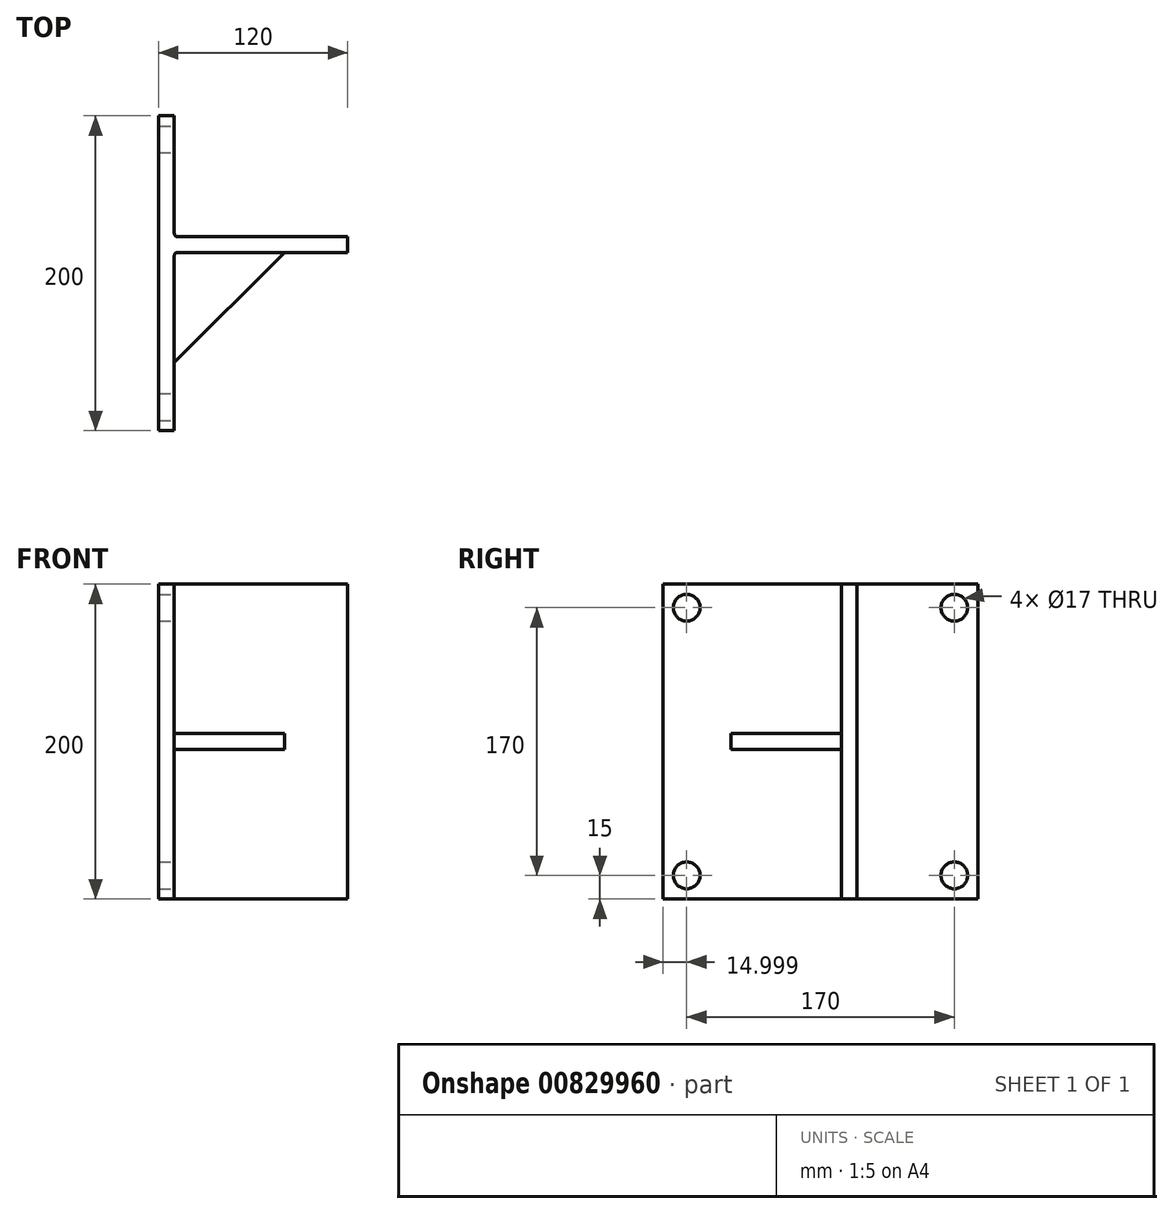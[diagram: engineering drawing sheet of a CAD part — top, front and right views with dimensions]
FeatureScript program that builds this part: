
annotation { "Feature Type Name" : "Feature", "Feature Type Description" : "" }
export const myFeature = defineFeature(function(context is Context, id is Id, definition is map)
    precondition{}
    {
        {
            var Q0;
            Q0=qCreatedBy(makeId("Top.planeOp"),FACE);
            var sketch = newSketch(context, id + "F0", { "sketchPlane" : qUnion([Q0])});
            skLineSegment(sketch, "E0", {"start": v(-22.94, 104.59) * mm, "end": v(-22.94, -95.41) * mm});
            skLineSegment(sketch, "E1", {"start": v(-22.94, -95.41) * mm, "end": v(-12.94, -95.41) * mm});
            skLineSegment(sketch, "E2", {"start": v(-12.94, -95.41) * mm, "end": v(-12.94, 17.79) * mm});
            skLineSegment(sketch, "E3", {"start": v(-12.94, 17.79) * mm, "end": v(97.06, 17.79) * mm});
            skLineSegment(sketch, "E4", {"start": v(-22.94, 104.59) * mm, "end": v(-12.94, 104.59) * mm});
            skLineSegment(sketch, "E5", {"start": v(97.06, 17.79) * mm, "end": v(97.06, 27.79) * mm});
            skLineSegment(sketch, "E6", {"start": v(97.06, 27.79) * mm, "end": v(-12.94, 27.79) * mm});
            skLineSegment(sketch, "E7", {"start": v(-12.94, 104.59) * mm, "end": v(-12.94, 27.79) * mm});
            skSolve(sketch);
        }
        {
            var Q0;
            Q0=makeQuery(id+"F0.imprint","IMPRINT",FACE,{"disambiguationData":[TD([[makeQuery(id+"F0.imprint","IMPRINT",EDGE,{"derivedFrom":sQuery(id+"F0.wireOp",EDGE,"E0")}),1.0]])]});
            extrude(context, id + "F1", {"entities" : qUnion([Q0]), "depth" : 200 * mm, "offsetDistance" : 25 * mm});
        }
        {
            var Q0;
            Q0=makeQuery(id+"F1.opExtrude","SWEPT_FACE",FACE,{"disambiguationData":[OSD([sQuery(id+"F0.wireOp",EDGE,"E7")])]});
            var sketch = newSketch(context, id + "F2", { "sketchPlane" : qUnion([Q0])});
            skPoint(sketch, "E8", {"position": v(89.59, 185) * mm});
            skPoint(sketch, "E9", {"position": v(89.59, 15) * mm});
            skPoint(sketch, "E10", {"position": v(-80.41, 185) * mm});
            skPoint(sketch, "E11", {"position": v(-80.41, 15) * mm});
            skCircle(sketch, "E12", {"center": v(89.59, 185) * mm, "radius": 8.5 * mm});
            skCircle(sketch, "E13", {"center": v(89.59, 15) * mm, "radius": 8.5 * mm});
            skCircle(sketch, "E14", {"center": v(-80.41, 15) * mm, "radius": 8.5 * mm});
            skCircle(sketch, "E15", {"center": v(-80.41, 185) * mm, "radius": 8.5 * mm});
            skSolve(sketch);
        }
        {
            var Q0;
            Q0=makeQuery(id+"F2.imprint","IMPRINT",FACE,{"disambiguationData":[TD([[makeQuery(id+"F2.imprint","IMPRINT",EDGE,{"derivedFrom":sQuery(id+"F2.wireOp",EDGE,"E12")}),1.0]])]});
            var Q1;
            Q1=makeQuery(id+"F2.imprint","IMPRINT",FACE,{"disambiguationData":[TD([[makeQuery(id+"F2.imprint","IMPRINT",EDGE,{"derivedFrom":sQuery(id+"F2.wireOp",EDGE,"E13")}),1.0]])]});
            var Q2;
            Q2=makeQuery(id+"F2.imprint","IMPRINT",FACE,{"disambiguationData":[TD([[makeQuery(id+"F2.imprint","IMPRINT",EDGE,{"derivedFrom":sQuery(id+"F2.wireOp",EDGE,"E14")}),1.0]])]});
            var Q3;
            Q3=makeQuery(id+"F2.imprint","IMPRINT",FACE,{"disambiguationData":[TD([[makeQuery(id+"F2.imprint","IMPRINT",EDGE,{"derivedFrom":sQuery(id+"F2.wireOp",EDGE,"E15")}),1.0]])]});
            extrude(context, id + "F3", {"entities" : qUnion([Q0, Q1, Q2, Q3]), "operationType" : NewBodyOperationType.REMOVE, "endBound" : BoundingType.THROUGH_ALL, "oppositeDirection" : true, "depth" : 25 * mm, "offsetDistance" : 25 * mm});
        }
        {
            var Q0;
            Q0=makeQuery(id+"F1.opExtrude","SWEPT_FACE",FACE,{"disambiguationData":[OSD([sQuery(id+"F0.wireOp",EDGE,"E2")])]});
            var sketch = newSketch(context, id + "F4", { "sketchPlane" : qUnion([Q0])});
            skLineSegment(sketch, "E16", {"start": v(17.79, 95) * mm, "end": v(-52.21, 95) * mm});
            skLineSegment(sketch, "E17", {"start": v(-52.21, 95) * mm, "end": v(-52.21, 105) * mm});
            skLineSegment(sketch, "E18", {"start": v(-52.21, 105) * mm, "end": v(17.79, 105) * mm});
            skLineSegment(sketch, "E19", {"start": v(17.79, 105) * mm, "end": v(17.79, 95) * mm});
            skSolve(sketch);
        }
        {
            var Q0;
            Q0=makeQuery(id+"F4.imprint","IMPRINT",FACE,{"disambiguationData":[TD([[makeQuery(id+"F4.imprint","IMPRINT",EDGE,{"derivedFrom":sQuery(id+"F4.wireOp",EDGE,"E16")}),-1.0]])]});
            extrude(context, id + "F5", {"entities" : qUnion([Q0]), "operationType" : NewBodyOperationType.ADD, "depth" : 70 * mm, "offsetDistance" : 25 * mm});
        }
        {
            var Q0;
            Q0=makeQuery(id+"F5.opExtrude","SWEPT_FACE",FACE,{"disambiguationData":[OSD([sQuery(id+"F4.wireOp",EDGE,"E18")])]});
            var sketch = newSketch(context, id + "F6", { "sketchPlane" : qUnion([Q0])});
            skLineSegment(sketch, "E20", {"start": v(-12.94, -52.21) * mm, "end": v(57.06, 17.79) * mm});
            skSolve(sketch);
        }
        {
            var Q0;
            Q0=makeQuery(id+"F6.imprint","IMPRINT",FACE,{"disambiguationData":[TD([[makeQuery(id+"F6.imprint","IMPRINT",EDGE,{"derivedFrom":sQuery(id+"F6.wireOp",EDGE,"E20")}),-1.0]])]});
            extrude(context, id + "F7", {"entities" : qUnion([Q0]), "operationType" : NewBodyOperationType.REMOVE, "oppositeDirection" : true, "depth" : 10 * mm, "offsetDistance" : 25 * mm});
        }
        {
            var Q0;
            {var subQ0=sQuery(id+"F0.wireOp",EDGE,"E3");var subQ1=sQuery(id+"F0.wireOp",EDGE,"E2");Q0=makeQuery(id+"F5.boolean.opBoolean","SPLIT",EDGE,{"disambiguationData":[TD([makeQuery(id+"F5.opExtrude","SWEPT_FACE",FACE,{"disambiguationData":[OSD([sQuery(id+"F4.wireOp",EDGE,"E18")])]})])],"derivedFrom":makeQuery(id+"F1.opExtrude","SWEPT_EDGE",EDGE,{"disambiguationData":[OSD([subQ1,subQ0])]})});}
            var Q1;
            Q1=makeQuery(id+"F5.opExtrude","CAP_EDGE",EDGE,{"disambiguationData":[OSD([sQuery(id+"F4.wireOp",EDGE,"E18")])],"isStart":true});
            var Q2;
            Q2=makeQuery(id+"F5.opExtrude","SWEPT_EDGE",EDGE,{"disambiguationData":[OSD([sQuery(id+"F0.wireOp",EDGE,"E2"),sQuery(id+"F0.wireOp",EDGE,"E3"),sQuery(id+"F4.wireOp",EDGE,"E18"),sQuery(id+"F4.wireOp",EDGE,"E19")])]});
            var Q3;
            Q3=makeQuery(id+"F5.opExtrude","CAP_EDGE",EDGE,{"disambiguationData":[OSD([sQuery(id+"F4.wireOp",EDGE,"E16")])],"isStart":true});
            var Q4;
            {var subQ0=sQuery(id+"F0.wireOp",EDGE,"E3");var subQ1=sQuery(id+"F0.wireOp",EDGE,"E2");Q4=makeQuery(id+"F5.boolean.opBoolean","SPLIT",EDGE,{"disambiguationData":[TD([makeQuery(id+"F5.opExtrude","SWEPT_FACE",FACE,{"disambiguationData":[OSD([sQuery(id+"F4.wireOp",EDGE,"E16")])]})])],"derivedFrom":makeQuery(id+"F1.opExtrude","SWEPT_EDGE",EDGE,{"disambiguationData":[OSD([subQ1,subQ0])]})});}
            var Q5;
            Q5=makeQuery(id+"F5.opExtrude","SWEPT_EDGE",EDGE,{"disambiguationData":[OSD([sQuery(id+"F0.wireOp",EDGE,"E2"),sQuery(id+"F0.wireOp",EDGE,"E3"),sQuery(id+"F4.wireOp",EDGE,"E16"),sQuery(id+"F4.wireOp",EDGE,"E19")])]});
            var Q6;
            Q6=makeQuery(id+"F1.opExtrude","SWEPT_EDGE",EDGE,{"disambiguationData":[OSD([sQuery(id+"F0.wireOp",EDGE,"E6"),sQuery(id+"F0.wireOp",EDGE,"E7")])]});
            var Q7;
            {var subQ0=sQuery(id+"F4.wireOp",EDGE,"E19");Q7=makeQuery(id+"F7.boolean.opBoolean","MERGE",EDGE,{"derivedFrom":[makeQuery(id+"F5.opExtrude","CAP_EDGE",EDGE,{"disambiguationData":[OSD([subQ0])],"isStart":false}),makeQuery(id+"F7.opExtrude","SWEPT_EDGE",EDGE,{"disambiguationData":[OSD([sQuery(id+"F0.wireOp",EDGE,"E2"),sQuery(id+"F0.wireOp",EDGE,"E3"),sQuery(id+"F4.wireOp",EDGE,"E18"),subQ0,sQuery(id+"F6.wireOp",EDGE,"E20")])]})]});}
            fillet(context, id + "F8", {"entities" : qUnion([Q0, Q1, Q2, Q3, Q4, Q5, Q6, Q7]), "radius" : 2 * mm, "tangentPropagation" : true, "allowEdgeOverflow" : false});
        }
    });
